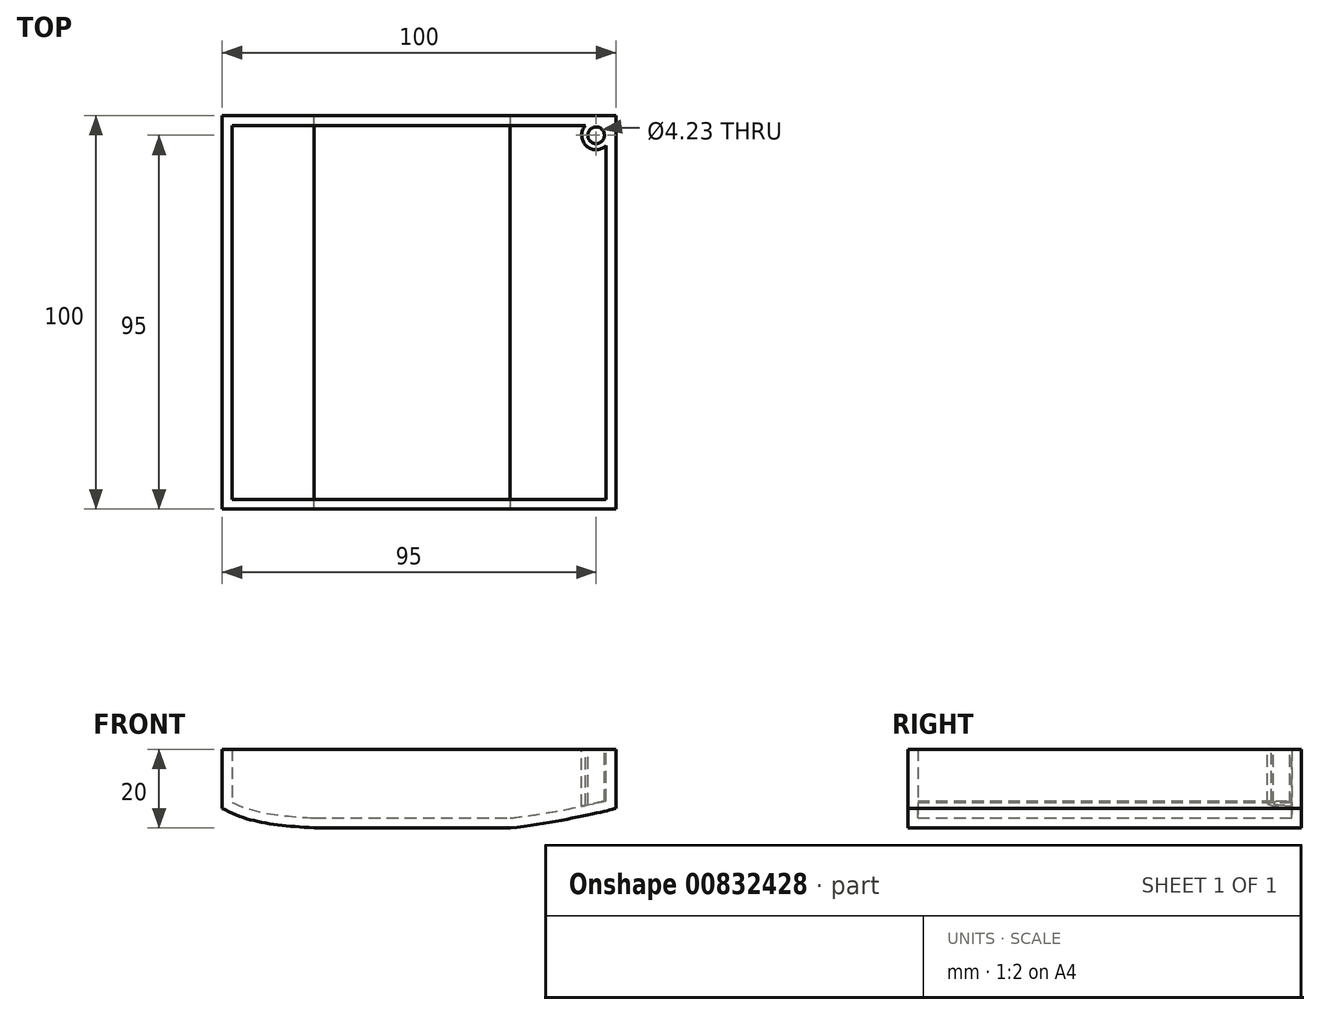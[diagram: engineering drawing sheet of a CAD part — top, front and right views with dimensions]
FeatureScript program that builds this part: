
annotation { "Feature Type Name" : "Feature", "Feature Type Description" : "" }
export const myFeature = defineFeature(function(context is Context, id is Id, definition is map)
    precondition{}
    {
        {
            var Q0;
            Q0=qCreatedBy(makeId("Front.planeOp"),FACE);
            var sketch = newSketch(context, id + "F0", { "sketchPlane" : qUnion([Q0])});
            skFitSpline(sketch, "E0", {"points": [v(-50, -5) * mm, v(-26.7, -10) * mm, v(23.3, -10) * mm, v(50.08, -5) * mm, v(49.81, -5.03) * mm], "startDerivative": vector(70.6, -40.72) * mm, "endDerivative": vector(-19.27, -3.31) * mm});
            skLineSegment(sketch, "E1.bottom", {"start": v(-50, 10) * mm, "end": v(50, 10) * mm});
            skLineSegment(sketch, "E1.top", {"start": v(-26.7, -10) * mm, "end": v(23.3, -10) * mm});
            skLineSegment(sketch, "E1.left", {"start": v(-50, 10) * mm, "end": v(-50, -5) * mm});
            skLineSegment(sketch, "E1.right", {"start": v(50, 10) * mm, "end": v(50, -5.03) * mm});
            skPoint(sketch, "E2.orphan", {"position": v(-50, -10) * mm});
            skPoint(sketch, "E3.orphan", {"position": v(50, -10) * mm});
            skSolve(sketch);
        }
        {
            var Q0;
            Q0=makeQuery(id+"F0.imprint","IMPRINT",FACE,{"disambiguationData":[TD([[makeQuery(id+"F0.imprint","IMPRINT",EDGE,{"derivedFrom":sQuery(id+"F0.wireOp",EDGE,"E0")}),1.0]])]});
            extrude(context, id + "F1", {"entities" : qUnion([Q0]), "depth" : 100 * mm, "offsetDistance" : 25 * mm});
        }
        {
            var Q0;
            Q0=makeQuery(id+"F1.opExtrude","SWEPT_FACE",FACE,{"disambiguationData":[OSD([sQuery(id+"F0.wireOp",EDGE,"E1.bottom")])]});
            shell(context, id + "F2", {"entities" : qUnion([Q0]), "thickness" : 2.5 * mm});
        }
        {
            var Q0;
            Q0=makeQuery(id+"F1.opExtrude","SWEPT_FACE",FACE,{"disambiguationData":[OSD([sQuery(id+"F0.wireOp",EDGE,"E1.bottom")])]});
            var sketch = newSketch(context, id + "F3", { "sketchPlane" : qUnion([Q0])});
            skCircle(sketch, "E4", {"center": v(45, -5) * mm, "radius": 2.11 * mm});
            skCircle(sketch, "E5", {"center": v(45, -5) * mm, "radius": 3.66 * mm});
            skSolve(sketch);
        }
        {
            var Q0;
            {var subQ0=sQuery(id+"F3.wireOp",EDGE,"E4");var subQ1=sQuery(id+"F0.wireOp",EDGE,"E1.bottom");var subQ2=makeQuery(id+"F2.opShell","OFFSET_EDGE",EDGE,{"disambiguationData":[OSD([subQ1]),TDD([makeQuery(id+"F1.opExtrude","CAP_EDGE",EDGE,{"disambiguationData":[OSD([subQ1])],"isStart":true})])]});var subQ3=makeQuery(id+"F3.imprint","INTERSECT",VERTEX,{"disambiguationData":[OD(1.0)],"derivedFrom":[subQ2,subQ0]});Q0=makeQuery(id+"F3.imprint","IMPRINT",FACE,{"disambiguationData":[TD([[makeQuery(id+"F3.imprint","IMPRINT",EDGE,{"disambiguationData":[TD([[subQ3,1.0]])],"derivedFrom":subQ2}),-1.0]])]});}
            var Q1;
            {var subQ0=sQuery(id+"F0.wireOp",EDGE,"E1.bottom");var subQ1=makeQuery(id+"F2.opShell","OFFSET_EDGE",EDGE,{"disambiguationData":[OSD([subQ0]),TDD([makeQuery(id+"F1.opExtrude","CAP_EDGE",EDGE,{"disambiguationData":[OSD([subQ0])],"isStart":true})])]});var subQ4=sQuery(id+"F3.wireOp",EDGE,"E4");var subQ6=makeQuery(id+"F3.imprint","INTERSECT",VERTEX,{"disambiguationData":[OD(0.0)],"derivedFrom":[subQ1,subQ4]});Q1=makeQuery(id+"F3.imprint","IMPRINT",FACE,{"disambiguationData":[TD([[makeQuery(id+"F3.imprint","IMPRINT",EDGE,{"disambiguationData":[TD([[subQ6,-1.0]])],"derivedFrom":subQ4}),-1.0]])]});}
            extrude(context, id + "F4", {"entities" : qUnion([Q0, Q1]), "operationType" : NewBodyOperationType.ADD, "endBound" : BoundingType.UP_TO_NEXT, "oppositeDirection" : true, "depth" : 25 * mm, "offsetDistance" : 25 * mm});
        }
    });
